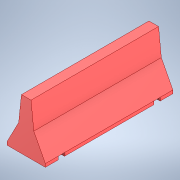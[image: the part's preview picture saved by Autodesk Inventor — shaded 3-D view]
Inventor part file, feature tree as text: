
AUTODESK INVENTOR PART (.ipt)
format: ipt  version: 2022 (Build 260153000, 153)  size: 243,200 bytes
history: native  units: in
note: dims shown in document units (in); Inventor stores cm internally (conversion verified against a paired STEP export)
features: extrude x5, sketch x5, chamfer x1
ambient origin geometry x8: Origin, YZ Plane, XZ Plane, XY Plane, X Axis, Y Axis, Z Axis, Center Point
bodies: Solid1 (feature_tree)
feature tree (11):
  extrude  "Extrusion1"  Depth=31.4961in
  extrude  "Extrusion5"  Depth=7.874in TaperAngle=0.0deg
  chamfer  "Chamfer1"  Distance=5.1181in Angle=45.0deg
  extrude  "Extrusion6"  Depth=3.937in
  sketch  "Sketch7"  dims[d44=1.9685in d45=3.937in]
  extrude  "Extrusion7"  Depth=3.937in
  extrude  "Extrusion8"  Depth=3.937in
  sketch  "Sketch1"  dims[d6=78.7402in d7=0.0in d28=31.4961in]
  sketch  "Sketch5"  dims[d35=70.8661in d36=7.874in d37=0.0in d38=5.1181in d39=0.0787in d40=45.0deg]
  sketch  "Sketch6"  dims[d41=15.748in d42=0.0in d43=3.937in]
  sketch  "Sketch8"  dims[d46=1.9685in d47=3.937in d48=1.9685in d49=3.937in d50=1.9685in d55=3.937in d56=1.9685in d57=3.937in d58=1.9685in d59=3.937in d60=1.9685in d61=3.937in d62=1.9685in d63=3.937in d64=0.0in d65=3.937in d66=0.0in]
